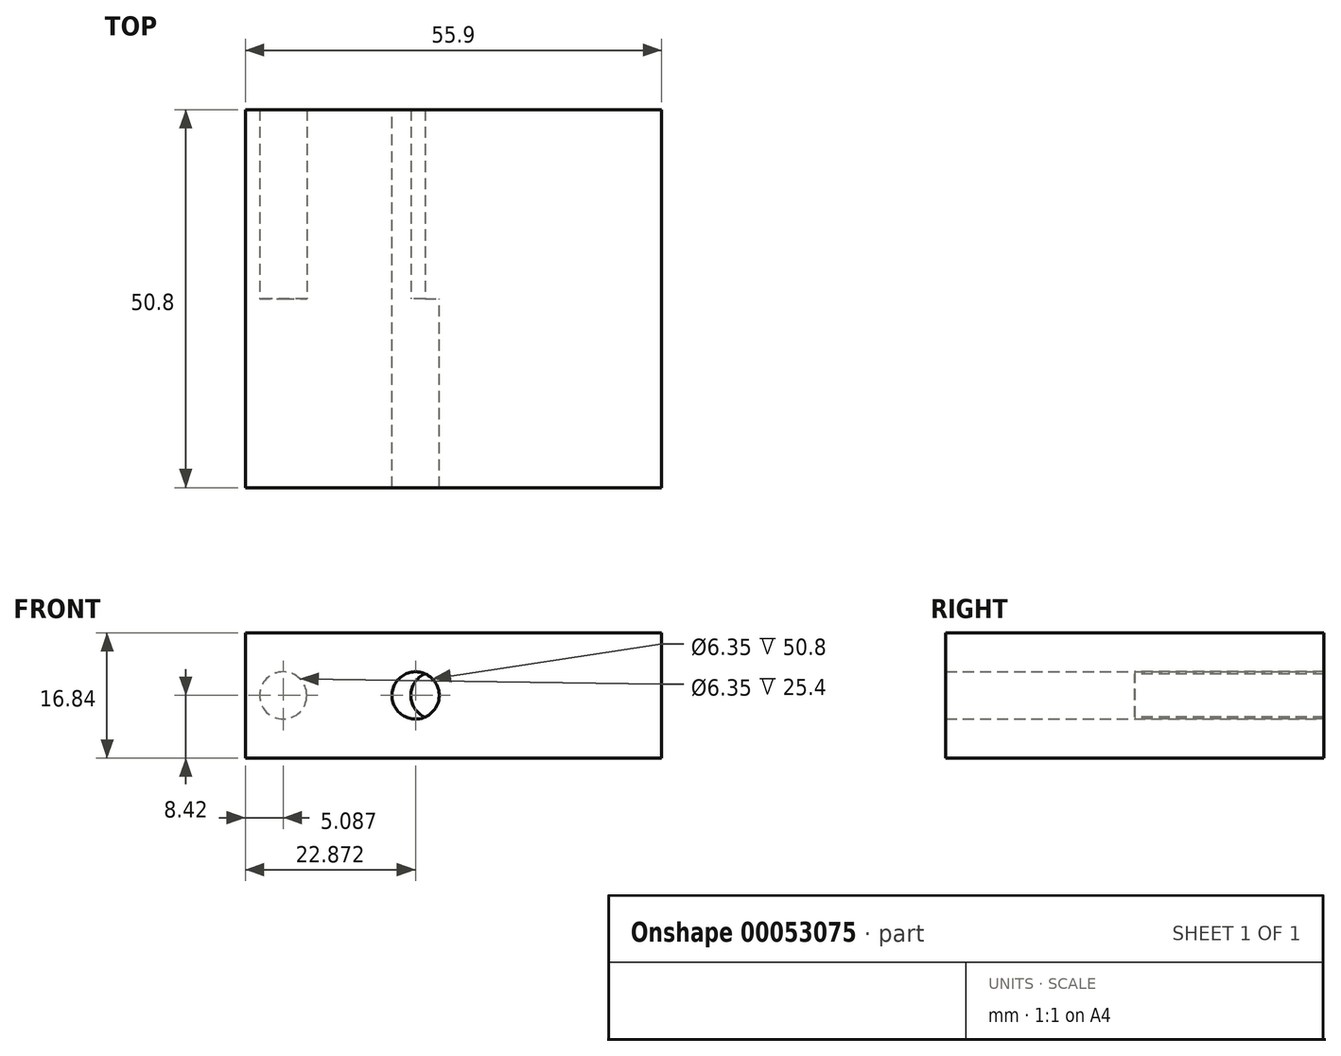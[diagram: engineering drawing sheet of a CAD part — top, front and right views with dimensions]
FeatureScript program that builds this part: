
annotation { "Feature Type Name" : "Feature", "Feature Type Description" : "" }
export const myFeature = defineFeature(function(context is Context, id is Id, definition is map)
    precondition{}
    {
        {
            var Q0;
            Q0=qCreatedBy(makeId("Front.planeOp"),FACE);
            var sketch = newSketch(context, id + "F0", { "sketchPlane" : qUnion([Q0])});
            skLineSegment(sketch, "E0.rect.bottom", {"start": v(-15.25, -8.42) * mm, "end": v(15.25, -8.42) * mm});
            skLineSegment(sketch, "E0.rect.top", {"start": v(-15.25, 8.42) * mm, "end": v(15.25, 8.42) * mm});
            skLineSegment(sketch, "E0.rect.left", {"start": v(-15.25, -8.42) * mm, "end": v(-15.25, 8.42) * mm});
            skLineSegment(sketch, "E0.rect.right", {"start": v(15.25, -8.42) * mm, "end": v(15.25, 8.42) * mm});
            skPoint(sketch, "E0.rect.middle", {"position": v(0, 0) * mm});
            skLineSegment(sketch, "E1", {"start": v(0, 8.42) * mm, "end": v(0, -8.42) * mm, "construction": true});
            skLineSegment(sketch, "E2", {"start": v(0, -8.42) * mm, "end": v(0, 0) * mm, "construction": true});
            skCircle(sketch, "E3", {"center": v(-7.62, 0) * mm, "radius": 3.18 * mm});
            skPoint(sketch, "E4.start.orphan", {"position": v(-7.62, 4.21) * mm});
            skPoint(sketch, "E5.orphan", {"position": v(-15.25, 0) * mm});
            skPoint(sketch, "E6.end.orphan", {"position": v(-7.62, -4.21) * mm});
            skCircle(sketch, "E7.MirrorC", {"center": v(7.62, 0) * mm, "radius": 3.18 * mm});
            skSolve(sketch);
        }
        {
            var Q0;
            Q0 = qSketchRegion(id + "F0", true);
            var Q1;
            Q1=makeQuery(id+"F0.imprint","IMPRINT",FACE,{"disambiguationData":[TD([[makeQuery(id+"F0.imprint","IMPRINT",EDGE,{"derivedFrom":sQuery(id+"F0.wireOp",EDGE,"E3")}),1.0]])]});
            var Q2;
            Q2=makeQuery(id+"F0.imprint","IMPRINT",FACE,{"disambiguationData":[TD([[makeQuery(id+"F0.imprint","IMPRINT",EDGE,{"derivedFrom":sQuery(id+"F0.wireOp",EDGE,"E7.MirrorC")}),-1.0]])]});
            var Q3;
            Q3 = qSketchRegion(id + "F2", true);
            extrude(context, id + "F1", {"entities" : qUnion([Q0, Q1, Q2, Q3]), "depth" : 25.4 * mm});
        }
        {
            var Q0;
            Q0=makeQuery(id+"F1.opExtrude","CAP_FACE",FACE,{"disambiguationData":[OSD([sQuery(id+"F0.wireOp",EDGE,"E0.rect.bottom"),sQuery(id+"F0.wireOp",EDGE,"E0.rect.top"),sQuery(id+"F0.wireOp",EDGE,"E0.rect.left"),sQuery(id+"F0.wireOp",EDGE,"E0.rect.right")])],"isStart":true});
            var sketch = newSketch(context, id + "F2", { "sketchPlane" : qUnion([Q0])});
            skLineSegment(sketch, "E8", {"start": v(0, 8.42) * mm, "end": v(0, -8.42) * mm, "construction": true});
            skLineSegment(sketch, "E9", {"start": v(0, -8.42) * mm, "end": v(0, 0) * mm, "construction": true});
            skLineSegment(sketch, "E10", {"start": v(0, 0) * mm, "end": v(-15.25, 0) * mm, "construction": true});
            skLineSegment(sketch, "E11", {"start": v(-15.25, 0) * mm, "end": v(0, 0) * mm, "construction": true});
            skLineSegment(sketch, "E12", {"start": v(-15.25, -8.42) * mm, "end": v(0, 0) * mm, "construction": true});
            skLineSegment(sketch, "E13", {"start": v(0, -8.42) * mm, "end": v(-15.25, 0) * mm, "construction": true});
            skLineSegment(sketch, "E14", {"start": v(0, 8.42) * mm, "end": v(-15.25, 0) * mm, "construction": true});
            skLineSegment(sketch, "E15", {"start": v(-15.25, 8.42) * mm, "end": v(0, 0) * mm, "construction": true});
            skLineSegment(sketch, "E16", {"start": v(-7.62, 4.21) * mm, "end": v(-15.25, -8.42) * mm, "construction": true});
            skLineSegment(sketch, "E17", {"start": v(-7.62, -4.21) * mm, "end": v(-15.25, 8.42) * mm, "construction": true});
            skCircle(sketch, "E18", {"center": v(-10.16, 0) * mm, "radius": 3.18 * mm});
            skCircle(sketch, "E19.MirrorC", {"center": v(10.16, 0) * mm, "radius": 3.18 * mm});
            skSolve(sketch);
        }
        {
            var Q0;
            Q0=makeQuery(id+"F2.imprint","IMPRINT",FACE,{"disambiguationData":[TD([[makeQuery(id+"F2.imprint","IMPRINT",EDGE,{"derivedFrom":sQuery(id+"F2.wireOp",EDGE,"E19.MirrorC")}),-1.0]])]});
            var Q1;
            Q1=makeQuery(id+"F2.imprint","IMPRINT",FACE,{"disambiguationData":[TD([[makeQuery(id+"F2.imprint","IMPRINT",EDGE,{"derivedFrom":sQuery(id+"F2.wireOp",EDGE,"E18")}),1.0]])]});
            extrude(context, id + "F3", {"entities" : qUnion([Q0, Q1]), "operationType" : NewBodyOperationType.ADD, "depth" : 25.4 * mm});
        }
        {
            var Q0;
            Q0=makeQuery(id+"F1.opExtrude","SWEPT_FACE",FACE,{"disambiguationData":[OSD([sQuery(id+"F0.wireOp",EDGE,"E0.rect.right")])]});
            extrude(context, id + "F4", {"entities" : qUnion([Q0]), "operationType" : NewBodyOperationType.ADD, "depth" : 25.4 * mm});
        }
    });
